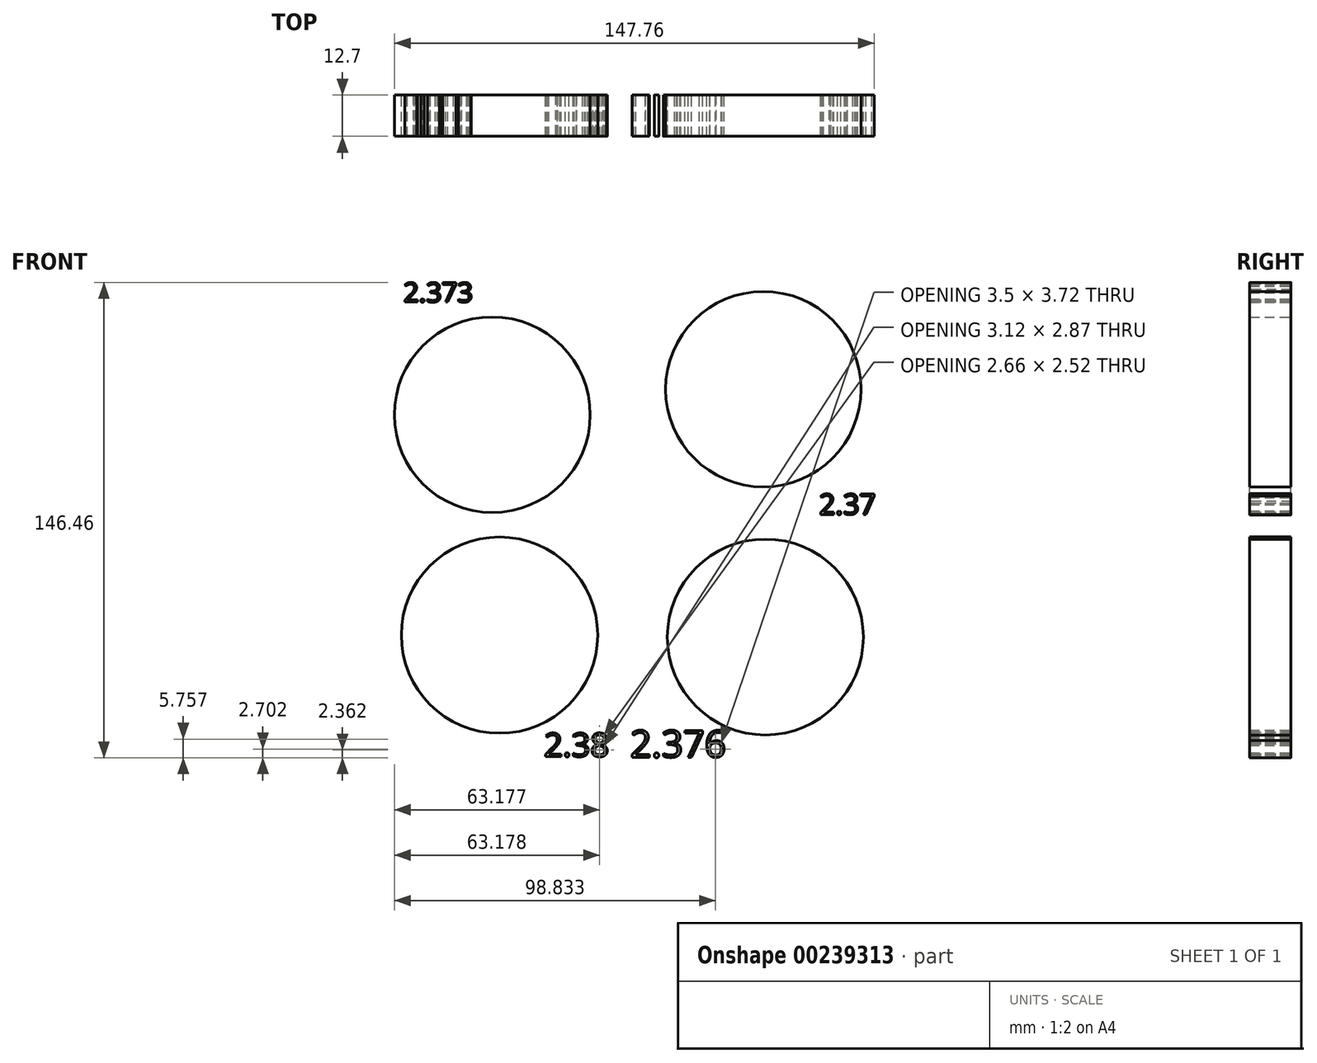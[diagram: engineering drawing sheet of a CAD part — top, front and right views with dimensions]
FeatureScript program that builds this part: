
annotation { "Feature Type Name" : "Feature", "Feature Type Description" : "" }
export const myFeature = defineFeature(function(context is Context, id is Id, definition is map)
    precondition{}
    {
        {
            var Q0;
            Q0=qCreatedBy(makeId("Front.planeOp"),FACE);
            var sketch = newSketch(context, id + "F0", { "sketchPlane" : qUnion([Q0])});
            skCircle(sketch, "E0", {"center": v(-42.43, 30.71) * mm, "radius": 30.14 * mm});
            skCircle(sketch, "E1", {"center": v(41.02, 38.6) * mm, "radius": 30.1 * mm});
            skCircle(sketch, "E2", {"center": v(-40.2, -37.18) * mm, "radius": 30.23 * mm});
            skCircle(sketch, "E3", {"center": v(41.62, -37.78) * mm, "radius": 30.18 * mm});
            skText(sketch, "E4", { "text": "2.37", "fontName": "OpenSans-Regular.ttf"});
            skText(sketch, "E5", { "text": "2.373\n", "fontName": "OpenSans-Regular.ttf"});
            skText(sketch, "E6", { "text": "2.38\n", "fontName": "OpenSans-Regular.ttf"});
            skText(sketch, "E7", { "text": "2.376", "fontName": "OpenSans-Regular.ttf"});
            const initialGuessF0  = {"E4": [0.05816, 0, 1, 0, 0.00635], "E5": [-0.06981, 0.06544, 1, 0, 0.00603], "E6": [-0.02653, -0.0746, 1, 0, 0.00728], "E7": [0, -0.0748, 1, 0, 0.00832]};
            skSetInitialGuess(sketch, initialGuessF0);
            skSolve(sketch);
        }
        {
            var Q0;
            Q0 = qSketchRegion(id + "F0", true);
            extrude(context, id + "F1", {"entities" : qUnion([Q0]), "depth" : 12.7 * mm});
        }
    });
